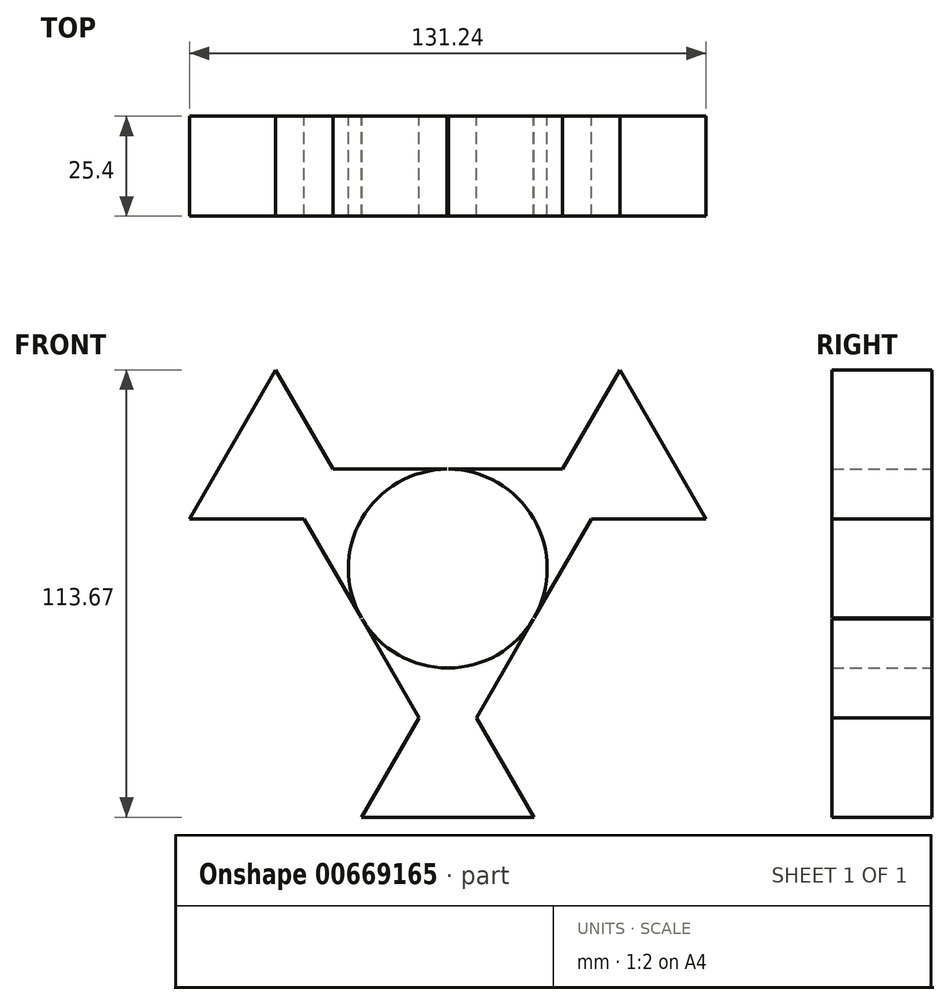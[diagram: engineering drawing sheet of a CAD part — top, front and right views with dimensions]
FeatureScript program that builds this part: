
annotation { "Feature Type Name" : "Feature", "Feature Type Description" : "" }
export const myFeature = defineFeature(function(context is Context, id is Id, definition is map)
    precondition{}
    {
        {
            var Q0;
            Q0=qCreatedBy(makeId("Front.planeOp"),FACE);
            var sketch = newSketch(context, id + "F0", { "sketchPlane" : qUnion([Q0])});
            skLineSegment(sketch, "E0.0", {"start": v(-43.75, 25.26) * mm, "end": v(43.75, 25.26) * mm});
            skLineSegment(sketch, "E0.1", {"start": v(43.75, 25.26) * mm, "end": v(0, -50.52) * mm});
            skLineSegment(sketch, "E0.2", {"start": v(0, -50.52) * mm, "end": v(-43.75, 25.26) * mm});
            skPoint(sketch, "E0.0.midPoint", {"position": v(0, 25.26) * mm});
            skCircle(sketch, "E1", {"center": v(0, 0) * mm, "radius": 25.26 * mm});
            skLineSegment(sketch, "E2.0", {"start": v(29.17, 0.17) * mm, "end": v(14.73, -25.17) * mm});
            skLineSegment(sketch, "E2.1", {"start": v(14.73, -25.17) * mm, "end": v(-14.44, -25.34) * mm});
            skLineSegment(sketch, "E2.2", {"start": v(-14.44, -25.34) * mm, "end": v(-29.17, -0.17) * mm});
            skLineSegment(sketch, "E2.3", {"start": v(-29.17, -0.17) * mm, "end": v(-14.73, 25.17) * mm});
            skLineSegment(sketch, "E2.4", {"start": v(-14.73, 25.17) * mm, "end": v(14.44, 25.34) * mm});
            skLineSegment(sketch, "E2.5", {"start": v(14.44, 25.34) * mm, "end": v(29.17, 0.17) * mm});
            skPoint(sketch, "E2.0.midPoint", {"position": v(21.95, -12.5) * mm});
            skLineSegment(sketch, "E3", {"start": v(0, 0) * mm, "end": v(43.75, 25.26) * mm});
            skLineSegment(sketch, "E4", {"start": v(0, 0) * mm, "end": v(-43.75, 25.26) * mm});
            skLineSegment(sketch, "E5", {"start": v(0, 0) * mm, "end": v(0, -50.52) * mm});
            skCircle(sketch, "E6.cCircle", {"center": v(43.75, 25.26) * mm, "radius": 25.26 * mm, "construction": true});
            skLineSegment(sketch, "E6.0", {"start": v(21.88, 12.63) * mm, "end": v(43.75, 50.52) * mm});
            skLineSegment(sketch, "E6.1", {"start": v(43.75, 50.52) * mm, "end": v(65.62, 12.63) * mm});
            skLineSegment(sketch, "E6.2", {"start": v(65.62, 12.63) * mm, "end": v(21.88, 12.63) * mm});
            skCircle(sketch, "E7.cCircle", {"center": v(-43.75, 25.26) * mm, "radius": 25.26 * mm, "construction": true});
            skLineSegment(sketch, "E7.0", {"start": v(-21.88, 12.63) * mm, "end": v(-65.62, 12.63) * mm});
            skLineSegment(sketch, "E7.1", {"start": v(-65.62, 12.63) * mm, "end": v(-43.75, 50.52) * mm});
            skLineSegment(sketch, "E7.2", {"start": v(-43.75, 50.52) * mm, "end": v(-21.88, 12.63) * mm});
            skCircle(sketch, "E8.cCircle", {"center": v(0, -50.52) * mm, "radius": 25.26 * mm, "construction": true});
            skLineSegment(sketch, "E8.0", {"start": v(0, -25.26) * mm, "end": v(21.87, -63.15) * mm});
            skLineSegment(sketch, "E8.1", {"start": v(21.87, -63.15) * mm, "end": v(-21.87, -63.15) * mm});
            skLineSegment(sketch, "E8.2", {"start": v(-21.87, -63.15) * mm, "end": v(0, -25.26) * mm});
            skSolve(sketch);
        }
        {
            var Q0;
            {var subQ0=sQuery(id+"F0.wireOp",EDGE,"E6.2");var subQ1=sQuery(id+"F0.wireOp",EDGE,"E0.1");var subQ2=makeQuery(id+"F0.imprint","INTERSECT",VERTEX,{"derivedFrom":[subQ1,subQ0]});Q0=makeQuery(id+"F0.imprint","IMPRINT",FACE,{"disambiguationData":[TD([[makeQuery(id+"F0.imprint","IMPRINT",EDGE,{"disambiguationData":[TD([[subQ2,-1.0]])],"derivedFrom":subQ1}),-1.0]])]});}
            var Q1;
            {var subQ0=sQuery(id+"F0.wireOp",EDGE,"E2.5");var subQ1=sQuery(id+"F0.wireOp",EDGE,"E0.0");var subQ2=makeQuery(id+"F0.imprint","INTERSECT",VERTEX,{"derivedFrom":[subQ1,subQ0]});Q1=makeQuery(id+"F0.imprint","IMPRINT",FACE,{"disambiguationData":[TD([[makeQuery(id+"F0.imprint","IMPRINT",EDGE,{"disambiguationData":[TD([[subQ2,-1.0]])],"derivedFrom":subQ1}),-1.0]])]});}
            var Q2;
            {var subQ1=sQuery(id+"F0.wireOp",EDGE,"E0.0");var subQ3=sQuery(id+"F0.wireOp",EDGE,"E6.0");var subQ4=makeQuery(id+"F0.imprint","INTERSECT",VERTEX,{"derivedFrom":[subQ1,subQ3]});Q2=makeQuery(id+"F0.imprint","IMPRINT",FACE,{"disambiguationData":[TD([[makeQuery(id+"F0.imprint","IMPRINT",EDGE,{"disambiguationData":[TD([[subQ4,-1.0]])],"derivedFrom":subQ1}),-1.0]])]});}
            var Q3;
            {var subQ1=sQuery(id+"F0.wireOp",EDGE,"E0.1");var subQ3=sQuery(id+"F0.wireOp",EDGE,"E6.2");var subQ4=makeQuery(id+"F0.imprint","INTERSECT",VERTEX,{"derivedFrom":[subQ1,subQ3]});Q3=makeQuery(id+"F0.imprint","IMPRINT",FACE,{"disambiguationData":[TD([[makeQuery(id+"F0.imprint","IMPRINT",EDGE,{"disambiguationData":[TD([[subQ4,1.0]])],"derivedFrom":subQ1}),-1.0]])]});}
            var Q4;
            {var subQ0=sQuery(id+"F0.wireOp",EDGE,"E6.1");Q4=makeQuery(id+"F0.imprint","IMPRINT",FACE,{"disambiguationData":[TD([[makeQuery(id+"F0.imprint","IMPRINT",EDGE,{"derivedFrom":subQ0}),-1.0]])]});}
            var Q5;
            {var subQ0=sQuery(id+"F0.wireOp",EDGE,"E3");var subQ1=sQuery(id+"F0.wireOp",EDGE,"E1");var subQ2=makeQuery(id+"F0.imprint","INTERSECT",VERTEX,{"derivedFrom":[subQ1,subQ0]});Q5=makeQuery(id+"F0.imprint","IMPRINT",FACE,{"disambiguationData":[TD([[makeQuery(id+"F0.imprint","IMPRINT",EDGE,{"disambiguationData":[TD([[subQ2,1.0]])],"derivedFrom":subQ1}),-1.0]])]});}
            var Q6;
            {var subQ0=sQuery(id+"F0.wireOp",EDGE,"E2.5");var subQ1=sQuery(id+"F0.wireOp",EDGE,"E0.0");var subQ2=makeQuery(id+"F0.imprint","INTERSECT",VERTEX,{"derivedFrom":[subQ1,subQ0]});Q6=makeQuery(id+"F0.imprint","IMPRINT",FACE,{"disambiguationData":[TD([[makeQuery(id+"F0.imprint","IMPRINT",EDGE,{"disambiguationData":[TD([[subQ2,1.0]])],"derivedFrom":subQ1}),-1.0]])]});}
            var Q7;
            {var subQ0=sQuery(id+"F0.wireOp",EDGE,"E4");var subQ1=sQuery(id+"F0.wireOp",EDGE,"E1");var subQ2=makeQuery(id+"F0.imprint","INTERSECT",VERTEX,{"derivedFrom":[subQ1,subQ0]});Q7=makeQuery(id+"F0.imprint","IMPRINT",FACE,{"disambiguationData":[TD([[makeQuery(id+"F0.imprint","IMPRINT",EDGE,{"disambiguationData":[TD([[subQ2,1.0]])],"derivedFrom":subQ1}),-1.0]])]});}
            var Q8;
            {var subQ0=sQuery(id+"F0.wireOp",EDGE,"E2.3");var subQ1=sQuery(id+"F0.wireOp",EDGE,"E0.2");var subQ2=makeQuery(id+"F0.imprint","INTERSECT",VERTEX,{"derivedFrom":[subQ1,subQ0]});Q8=makeQuery(id+"F0.imprint","IMPRINT",FACE,{"disambiguationData":[TD([[makeQuery(id+"F0.imprint","IMPRINT",EDGE,{"disambiguationData":[TD([[subQ2,1.0]])],"derivedFrom":subQ1}),-1.0]])]});}
            var Q9;
            {var subQ3=sQuery(id+"F0.wireOp",EDGE,"E2.2");var subQ5=sQuery(id+"F0.wireOp",EDGE,"E2.1");var subQ6=makeQuery(id+"F0.imprint","INTERSECT",VERTEX,{"derivedFrom":[subQ5,subQ3]});Q9=makeQuery(id+"F0.imprint","IMPRINT",FACE,{"disambiguationData":[TD([[makeQuery(id+"F0.imprint","IMPRINT",EDGE,{"disambiguationData":[TD([[subQ6,1.0]])],"derivedFrom":subQ5}),-1.0]])]});}
            var Q10;
            {var subQ0=sQuery(id+"F0.wireOp",EDGE,"E2.1");var subQ1=sQuery(id+"F0.wireOp",EDGE,"E0.1");var subQ2=makeQuery(id+"F0.imprint","INTERSECT",VERTEX,{"derivedFrom":[subQ1,subQ0]});Q10=makeQuery(id+"F0.imprint","IMPRINT",FACE,{"disambiguationData":[TD([[makeQuery(id+"F0.imprint","IMPRINT",EDGE,{"disambiguationData":[TD([[subQ2,1.0]])],"derivedFrom":subQ1}),-1.0]])]});}
            var Q11;
            {var subQ0=sQuery(id+"F0.wireOp",EDGE,"E2.1");var subQ1=sQuery(id+"F0.wireOp",EDGE,"E0.1");var subQ2=makeQuery(id+"F0.imprint","INTERSECT",VERTEX,{"derivedFrom":[subQ1,subQ0]});Q11=makeQuery(id+"F0.imprint","IMPRINT",FACE,{"disambiguationData":[TD([[makeQuery(id+"F0.imprint","IMPRINT",EDGE,{"disambiguationData":[TD([[subQ2,-1.0]])],"derivedFrom":subQ1}),-1.0]])]});}
            var Q12;
            {var subQ3=sQuery(id+"F0.wireOp",EDGE,"E2.2");var subQ5=sQuery(id+"F0.wireOp",EDGE,"E2.1");var subQ7=makeQuery(id+"F0.imprint","INTERSECT",VERTEX,{"derivedFrom":[subQ5,subQ3]});Q12=makeQuery(id+"F0.imprint","IMPRINT",FACE,{"disambiguationData":[TD([[makeQuery(id+"F0.imprint","IMPRINT",EDGE,{"disambiguationData":[TD([[subQ7,1.0]])],"derivedFrom":subQ5}),1.0]])]});}
            var Q13;
            {var subQ3=sQuery(id+"F0.wireOp",EDGE,"E8.0");var subQ5=sQuery(id+"F0.wireOp",EDGE,"E2.1");var subQ7=makeQuery(id+"F0.imprint","INTERSECT",VERTEX,{"derivedFrom":[subQ5,subQ3]});Q13=makeQuery(id+"F0.imprint","IMPRINT",FACE,{"disambiguationData":[TD([[makeQuery(id+"F0.imprint","IMPRINT",EDGE,{"disambiguationData":[TD([[subQ7,-1.0]])],"derivedFrom":subQ5}),1.0]])]});}
            var Q14;
            {var subQ0=sQuery(id+"F0.wireOp",EDGE,"E5");var subQ5=sQuery(id+"F0.wireOp",EDGE,"E2.1");var subQ6=makeQuery(id+"F0.imprint","INTERSECT",VERTEX,{"derivedFrom":[subQ5,subQ0]});Q14=makeQuery(id+"F0.imprint","IMPRINT",FACE,{"disambiguationData":[TD([[makeQuery(id+"F0.imprint","IMPRINT",EDGE,{"disambiguationData":[TD([[subQ6,-1.0]])],"derivedFrom":subQ5}),1.0]])]});}
            var Q15;
            {var subQ0=sQuery(id+"F0.wireOp",EDGE,"E8.1");Q15=makeQuery(id+"F0.imprint","IMPRINT",FACE,{"disambiguationData":[TD([[makeQuery(id+"F0.imprint","IMPRINT",EDGE,{"derivedFrom":subQ0}),-1.0]])]});}
            var Q16;
            {var subQ0=sQuery(id+"F0.wireOp",EDGE,"E7.2");var subQ1=sQuery(id+"F0.wireOp",EDGE,"E0.0");var subQ2=makeQuery(id+"F0.imprint","INTERSECT",VERTEX,{"derivedFrom":[subQ1,subQ0]});Q16=makeQuery(id+"F0.imprint","IMPRINT",FACE,{"disambiguationData":[TD([[makeQuery(id+"F0.imprint","IMPRINT",EDGE,{"disambiguationData":[TD([[subQ2,-1.0]])],"derivedFrom":subQ1}),-1.0]])]});}
            var Q17;
            {var subQ0=sQuery(id+"F0.wireOp",EDGE,"E2.3");var subQ1=sQuery(id+"F0.wireOp",EDGE,"E0.2");var subQ2=makeQuery(id+"F0.imprint","INTERSECT",VERTEX,{"derivedFrom":[subQ1,subQ0]});Q17=makeQuery(id+"F0.imprint","IMPRINT",FACE,{"disambiguationData":[TD([[makeQuery(id+"F0.imprint","IMPRINT",EDGE,{"disambiguationData":[TD([[subQ2,-1.0]])],"derivedFrom":subQ1}),-1.0]])]});}
            var Q18;
            {var subQ1=sQuery(id+"F0.wireOp",EDGE,"E0.2");var subQ3=sQuery(id+"F0.wireOp",EDGE,"E7.0");var subQ4=makeQuery(id+"F0.imprint","INTERSECT",VERTEX,{"derivedFrom":[subQ1,subQ3]});Q18=makeQuery(id+"F0.imprint","IMPRINT",FACE,{"disambiguationData":[TD([[makeQuery(id+"F0.imprint","IMPRINT",EDGE,{"disambiguationData":[TD([[subQ4,-1.0]])],"derivedFrom":subQ1}),-1.0]])]});}
            var Q19;
            {var subQ1=sQuery(id+"F0.wireOp",EDGE,"E0.0");var subQ3=sQuery(id+"F0.wireOp",EDGE,"E7.2");var subQ4=makeQuery(id+"F0.imprint","INTERSECT",VERTEX,{"derivedFrom":[subQ1,subQ3]});Q19=makeQuery(id+"F0.imprint","IMPRINT",FACE,{"disambiguationData":[TD([[makeQuery(id+"F0.imprint","IMPRINT",EDGE,{"disambiguationData":[TD([[subQ4,1.0]])],"derivedFrom":subQ1}),-1.0]])]});}
            var Q20;
            {var subQ0=sQuery(id+"F0.wireOp",EDGE,"E7.1");Q20=makeQuery(id+"F0.imprint","IMPRINT",FACE,{"disambiguationData":[TD([[makeQuery(id+"F0.imprint","IMPRINT",EDGE,{"derivedFrom":subQ0}),-1.0]])]});}
            extrude(context, id + "F1", {"entities" : qUnion([Q0, Q1, Q2, Q3, Q4, Q5, Q6, Q7, Q8, Q9, Q10, Q11, Q12, Q13, Q14, Q15, Q16, Q17, Q18, Q19, Q20]), "depth" : 25.4 * mm, "offsetDistance" : 25.4 * mm});
        }
    });
